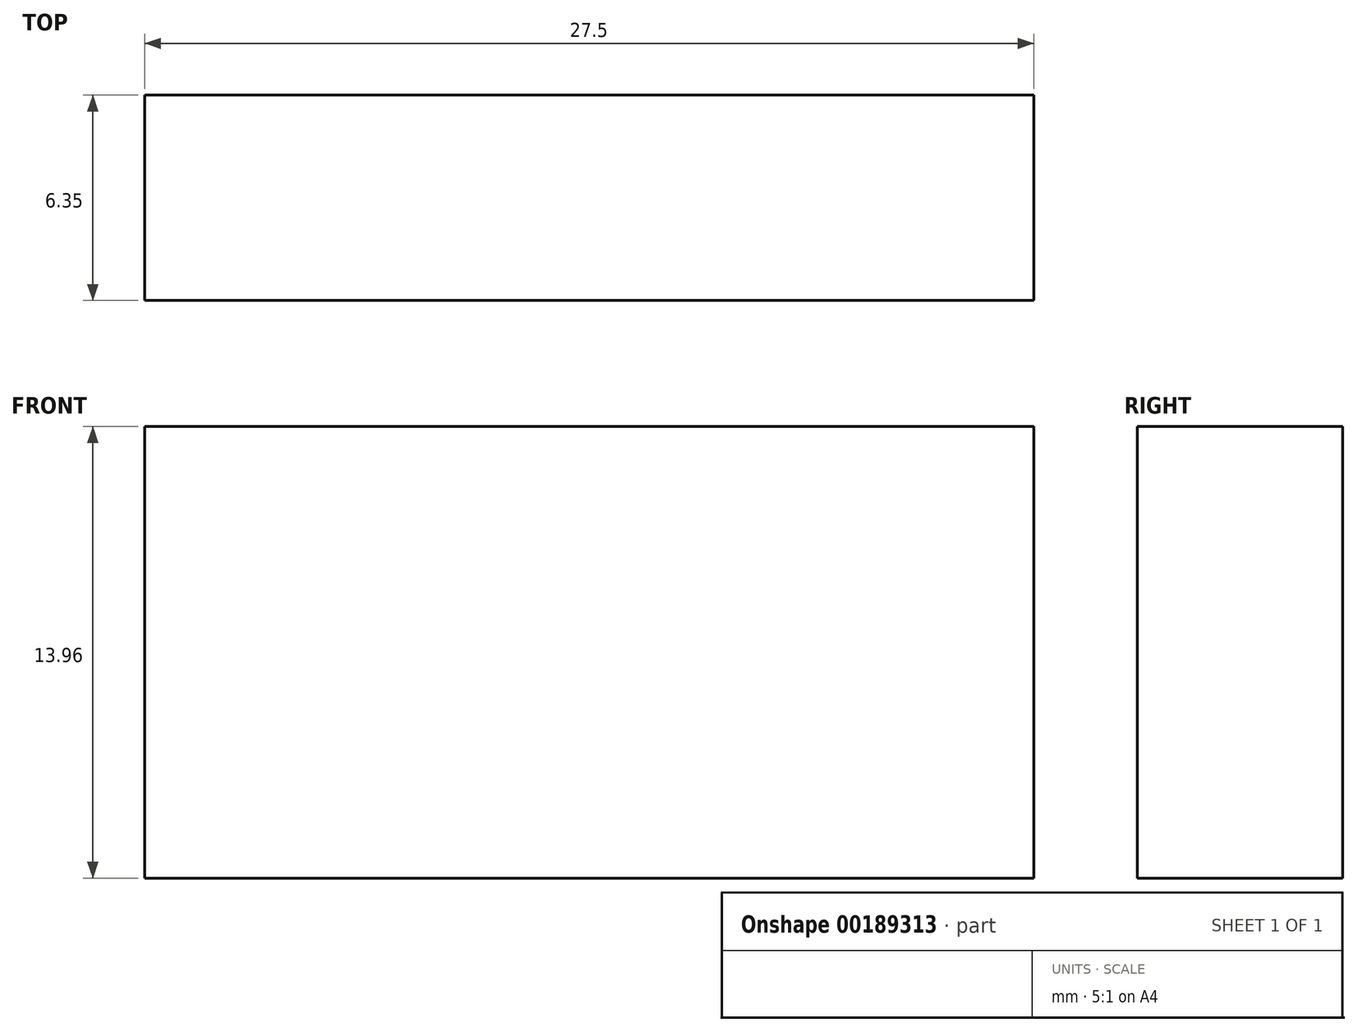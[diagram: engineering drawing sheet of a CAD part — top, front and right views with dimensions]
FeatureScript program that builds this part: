
annotation { "Feature Type Name" : "Feature", "Feature Type Description" : "" }
export const myFeature = defineFeature(function(context is Context, id is Id, definition is map)
    precondition{}
    {
        {
            var Q0;
            Q0=qCreatedBy(makeId("Front.planeOp"),FACE);
            var sketch = newSketch(context, id + "F0", { "sketchPlane" : qUnion([Q0])});
            skLineSegment(sketch, "E0.bottom", {"start": v(13.75, 6.98) * mm, "end": v(-13.75, 6.98) * mm});
            skLineSegment(sketch, "E0.top", {"start": v(13.75, -6.98) * mm, "end": v(-13.75, -6.98) * mm});
            skLineSegment(sketch, "E0.left", {"start": v(13.75, 6.98) * mm, "end": v(13.75, -6.98) * mm});
            skLineSegment(sketch, "E0.right", {"start": v(-13.75, 6.98) * mm, "end": v(-13.75, -6.98) * mm});
            skPoint(sketch, "E0.middle", {"position": v(0, 0) * mm});
            skSolve(sketch);
        }
        {
            var Q0;
            Q0=makeQuery(id+"F0.imprint","IMPRINT",FACE,{"disambiguationData":[TD([[makeQuery(id+"F0.imprint","IMPRINT",EDGE,{"derivedFrom":sQuery(id+"F0.wireOp",EDGE,"E0.bottom")}),1.0]])]});
            extrude(context, id + "F1", {"entities" : qUnion([Q0]), "depth" : 6.35 * mm});
        }
    });
